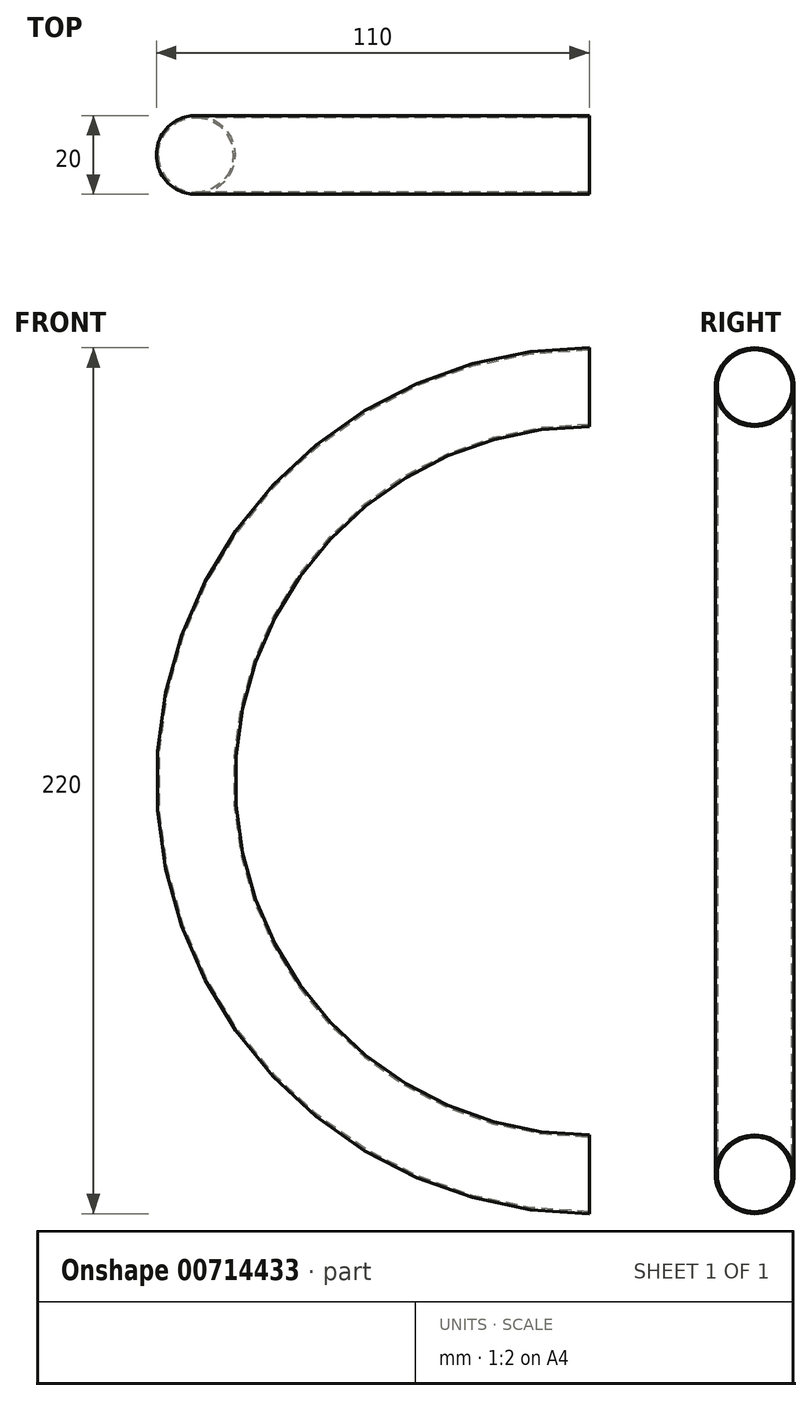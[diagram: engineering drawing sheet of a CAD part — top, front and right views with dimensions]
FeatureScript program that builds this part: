
annotation { "Feature Type Name" : "Feature", "Feature Type Description" : "" }
export const myFeature = defineFeature(function(context is Context, id is Id, definition is map)
    precondition{}
    {
        {
            var Q0;
            Q0=qCreatedBy(makeId("Right.planeOp"),FACE);
            var sketch = newSketch(context, id + "F0", { "sketchPlane" : qUnion([Q0])});
            skCircle(sketch, "E0", {"center": v(0, 0) * mm, "radius": 10 * mm});
            skCircle(sketch, "E1", {"center": v(0, 0) * mm, "radius": 9.5 * mm});
            skSolve(sketch);
        }
        {
            var Q0;
            Q0=qCreatedBy(makeId("Front.planeOp"),FACE);
            var sketch = newSketch(context, id + "F1", { "sketchPlane" : qUnion([Q0])});
            skArc(sketch, "E2", {"start": v(0, 200) * mm, "mid": v(-100, 100) * mm, "end": v(0, 0) * mm});
            skSolve(sketch);
        }
        {
            var Q0;
            Q0 = qSketchRegion(id + "F0", true);
            var Q1;
            Q1 = qConstructionFilter(qBodyType(qCreatedBy(id + "F1" ,EDGE), BodyType.WIRE), ConstructionObject.NO);
            sweep(context, id + "F2", {"profiles" : qUnion([Q0]), "path" : qUnion([Q1])});
        }
    });
